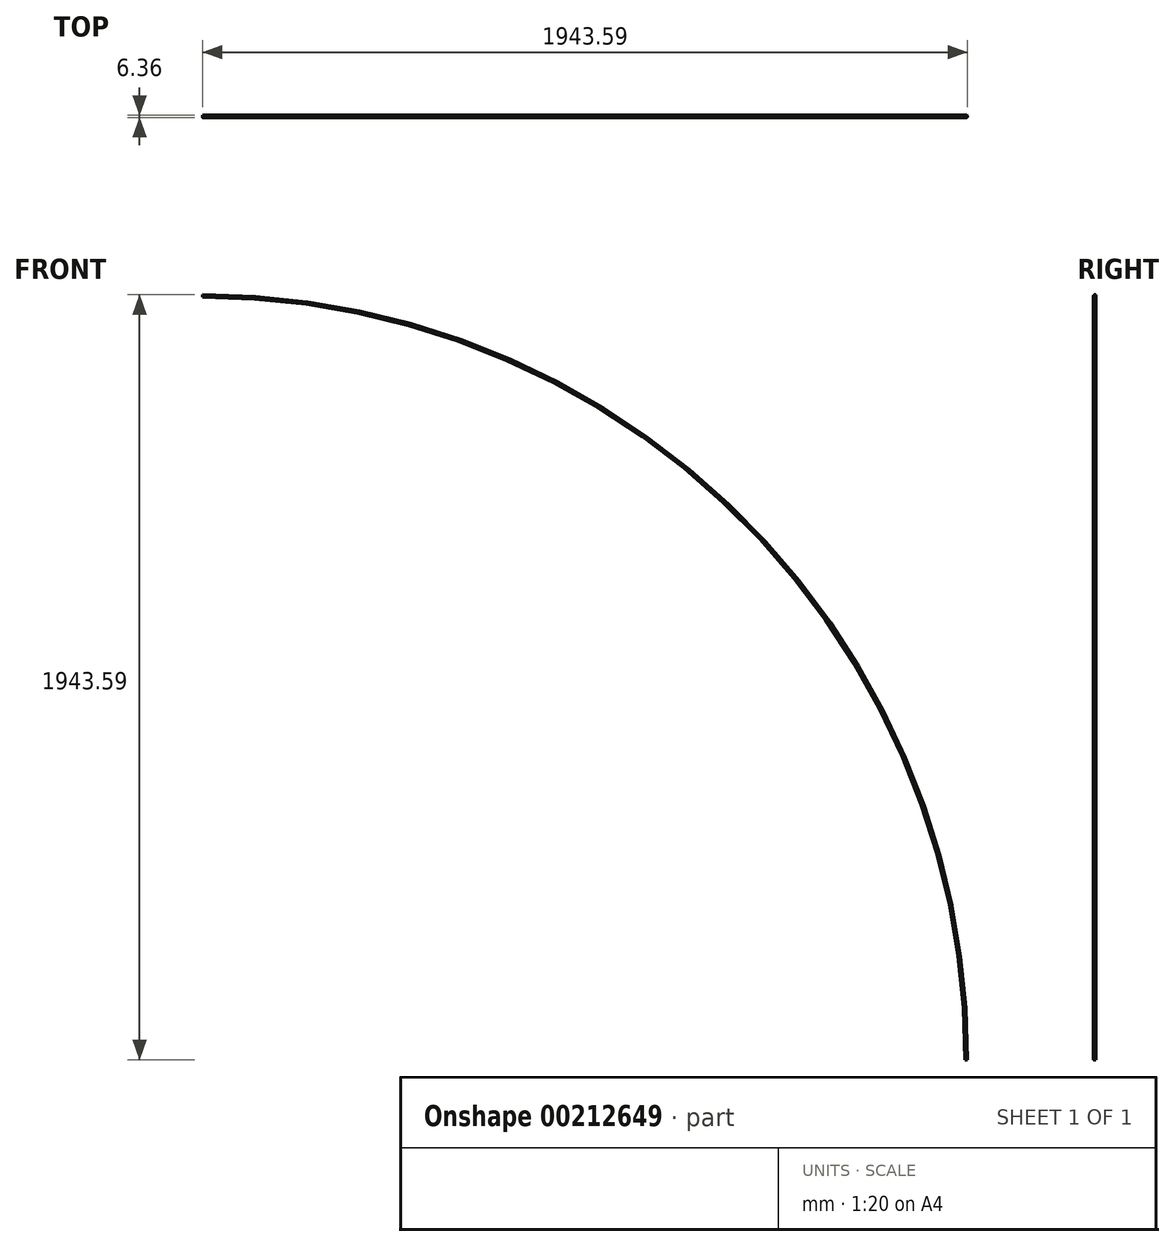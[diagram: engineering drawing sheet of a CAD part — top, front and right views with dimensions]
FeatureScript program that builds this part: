
annotation { "Feature Type Name" : "Feature", "Feature Type Description" : "" }
export const myFeature = defineFeature(function(context is Context, id is Id, definition is map)
    precondition{}
    {
        {
            var Q0;
            Q0=qCreatedBy(makeId("Front.planeOp"),FACE);
            var sketch = newSketch(context, id + "F0", { "sketchPlane" : qUnion([Q0])});
            skArc(sketch, "E0", {"start": v(1940.42, 0) * mm, "mid": v(1372.08, 1372.08) * mm, "end": v(0, 1940.42) * mm});
            skSolve(sketch);
        }
        {
            var Q0;
            Q0=qCreatedBy(makeId("Right.planeOp"),FACE);
            var sketch = newSketch(context, id + "F1", { "sketchPlane" : qUnion([Q0])});
            skCircle(sketch, "E1", {"center": v(0, 1940.42) * mm, "radius": 3.18 * mm});
            skSolve(sketch);
        }
        {
            var Q0;
            Q0=makeQuery(id+"F1.imprint","IMPRINT",FACE,{"disambiguationData":[TD([[makeQuery(id+"F1.imprint","IMPRINT",EDGE,{"derivedFrom":sQuery(id+"F1.wireOp",EDGE,"E1")}),1.0]])]});
            var Q1;
            Q1=sQuery(id+"F0.wireOp",EDGE,"E0");
            sweep(context, id + "F2", {"profiles" : qUnion([Q0]), "path" : qUnion([Q1])});
        }
    });
